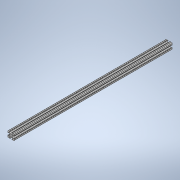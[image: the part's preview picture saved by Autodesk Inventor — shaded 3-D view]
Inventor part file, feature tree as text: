
AUTODESK INVENTOR PART (.ipt)
format: ipt  version: 2020 (Build 240168000, 168)  size: 240,640 bytes
history: native  units: in
note: dims shown in document units (in); Inventor stores cm internally (conversion verified against a paired STEP export)
features: extrude x1, sketch x1
ambient origin geometry x8: Origin, YZ Plane, XZ Plane, XY Plane, X Axis, Y Axis, Z Axis, Center Point
bodies: Solid1 (feature_tree)
feature tree (2):
  extrude  "Extrusion1"  [1 undecoded]
  sketch  "Sketch1"  dims[d0=25.0in d1=0.0in]
note: 1 required parameter value undecoded (feature->parameter linkage not recoverable at this tier; creation-order binding heuristic only, values carry confidence <= 0.55)
